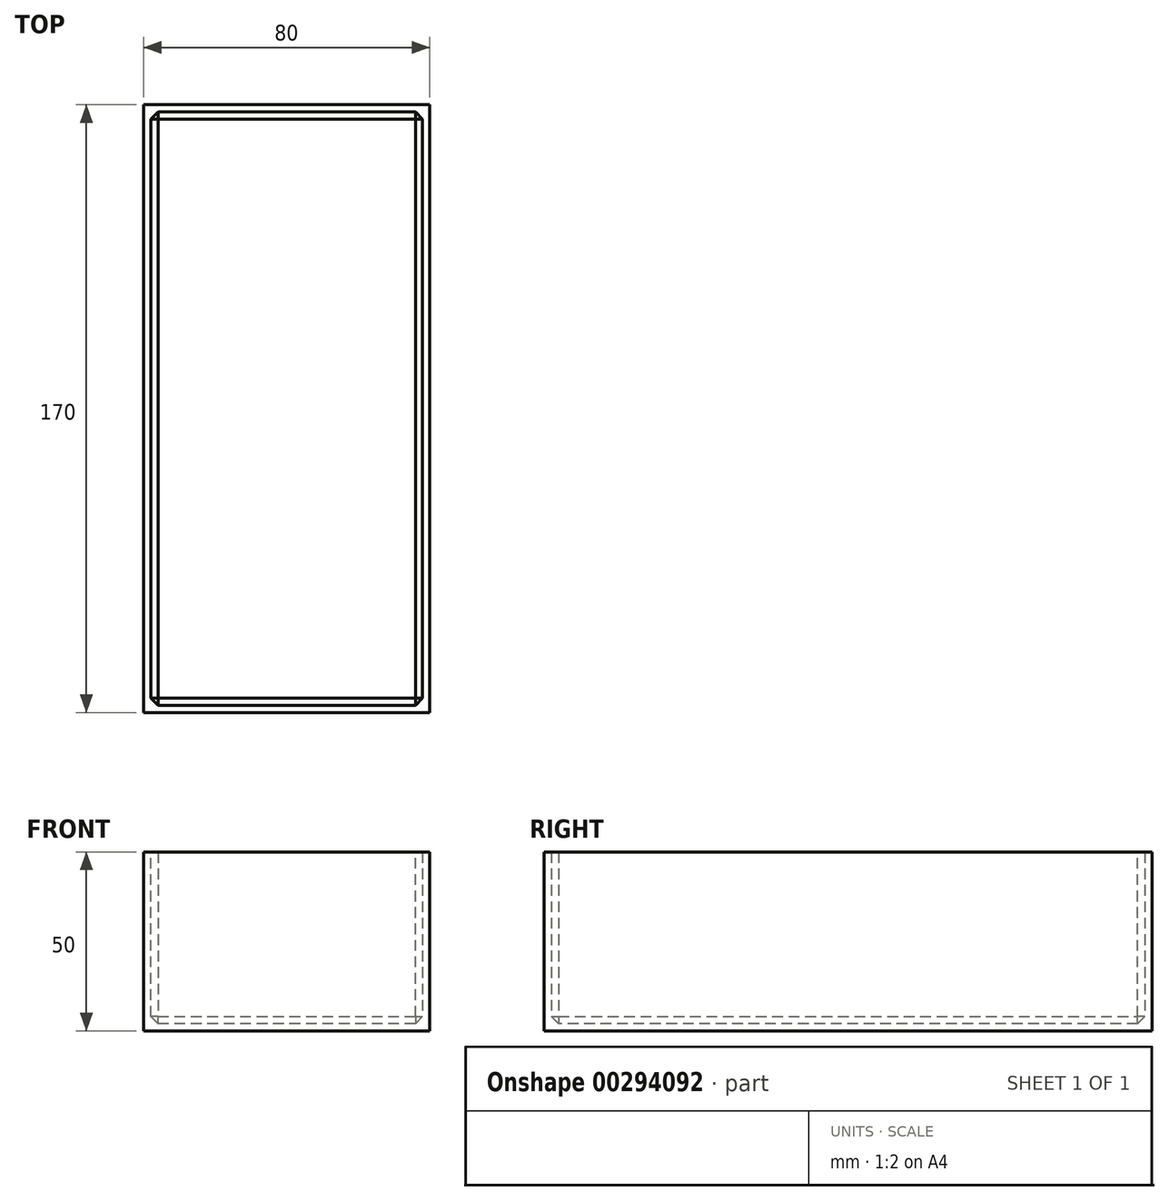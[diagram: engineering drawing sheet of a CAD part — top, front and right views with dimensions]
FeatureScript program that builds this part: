
annotation { "Feature Type Name" : "Feature", "Feature Type Description" : "" }
export const myFeature = defineFeature(function(context is Context, id is Id, definition is map)
    precondition{}
    {
        {
            assignVariable(context, id + "F0", {"name" : "BoxHeight", "anyValue" : 50 * mm});
        }
        {
            var Q0;
            Q0=qCreatedBy(makeId("Top.planeOp"),FACE);
            var sketch = newSketch(context, id + "F1", { "sketchPlane" : qUnion([Q0])});
            skLineSegment(sketch, "E0.bottom", {"start": v(-40, 85) * mm, "end": v(40, 85) * mm});
            skLineSegment(sketch, "E0.top", {"start": v(-40, -85) * mm, "end": v(40, -85) * mm});
            skLineSegment(sketch, "E0.left", {"start": v(-40, 85) * mm, "end": v(-40, -85) * mm});
            skLineSegment(sketch, "E0.right", {"start": v(40, 85) * mm, "end": v(40, -85) * mm});
            skPoint(sketch, "E0.middle", {"position": v(0, 0) * mm});
            skLineSegment(sketch, "E1.0", {"start": v(-38, 83) * mm, "end": v(38, 83) * mm});
            skLineSegment(sketch, "E1.1", {"start": v(-38, 83) * mm, "end": v(-38, -83) * mm});
            skLineSegment(sketch, "E1.2", {"start": v(-38, -83) * mm, "end": v(38, -83) * mm});
            skLineSegment(sketch, "E1.3", {"start": v(38, 83) * mm, "end": v(38, -83) * mm});
            skSolve(sketch);
        }
        {
            var Q0;
            Q0=makeQuery(id+"F1.imprint","IMPRINT",FACE,{"disambiguationData":[TD([[makeQuery(id+"F1.imprint","IMPRINT",EDGE,{"derivedFrom":sQuery(id+"F1.wireOp",EDGE,"E0.bottom")}),-1.0]])]});
            extrude(context, id + "F2", {"entities" : qUnion([Q0]), "depth" : getVariable(context, 'BoxHeight')});
        }
        {
            var Q0;
            Q0=qSketchRegion(id+"F1",true);
            var Q1;
            Q1=makeQuery(id+"F1.imprint","IMPRINT",FACE,{"disambiguationData":[TD([[makeQuery(id+"F1.imprint","IMPRINT",EDGE,{"derivedFrom":sQuery(id+"F1.wireOp",EDGE,"E1.0")}),-1.0]])]});
            extrude(context, id + "F3", {"entities" : qUnion([Q0, Q1]), "operationType" : NewBodyOperationType.ADD, "depth" : 2 * mm});
        }
        {
            var Q0;
            Q0=makeQuery(id+"F3.boolean.opBoolean","INTERSECT",EDGE,{"derivedFrom":[makeQuery(id+"F2.opExtrude","SWEPT_FACE",FACE,{"disambiguationData":[OSD([sQuery(id+"F1.wireOp",EDGE,"E1.0")])]}),makeQuery(id+"F3.opExtrude","CAP_FACE",FACE,{"disambiguationData":[OSD([sQuery(id+"F1.wireOp",EDGE,"E0.bottom"),sQuery(id+"F1.wireOp",EDGE,"E0.top"),sQuery(id+"F1.wireOp",EDGE,"E0.left"),sQuery(id+"F1.wireOp",EDGE,"E0.right")])],"isStart":false})]});
            var Q1;
            Q1=makeQuery(id+"F3.boolean.opBoolean","INTERSECT",EDGE,{"derivedFrom":[makeQuery(id+"F2.opExtrude","SWEPT_FACE",FACE,{"disambiguationData":[OSD([sQuery(id+"F1.wireOp",EDGE,"E1.3")])]}),makeQuery(id+"F3.opExtrude","CAP_FACE",FACE,{"disambiguationData":[OSD([sQuery(id+"F1.wireOp",EDGE,"E0.bottom"),sQuery(id+"F1.wireOp",EDGE,"E0.top"),sQuery(id+"F1.wireOp",EDGE,"E0.left"),sQuery(id+"F1.wireOp",EDGE,"E0.right")])],"isStart":false})]});
            var Q2;
            Q2=makeQuery(id+"F3.boolean.opBoolean","INTERSECT",EDGE,{"derivedFrom":[makeQuery(id+"F2.opExtrude","SWEPT_FACE",FACE,{"disambiguationData":[OSD([sQuery(id+"F1.wireOp",EDGE,"E1.1")])]}),makeQuery(id+"F3.opExtrude","CAP_FACE",FACE,{"disambiguationData":[OSD([sQuery(id+"F1.wireOp",EDGE,"E0.bottom"),sQuery(id+"F1.wireOp",EDGE,"E0.top"),sQuery(id+"F1.wireOp",EDGE,"E0.left"),sQuery(id+"F1.wireOp",EDGE,"E0.right")])],"isStart":false})]});
            var Q3;
            Q3=makeQuery(id+"F3.boolean.opBoolean","INTERSECT",EDGE,{"derivedFrom":[makeQuery(id+"F2.opExtrude","SWEPT_FACE",FACE,{"disambiguationData":[OSD([sQuery(id+"F1.wireOp",EDGE,"E1.2")])]}),makeQuery(id+"F3.opExtrude","CAP_FACE",FACE,{"disambiguationData":[OSD([sQuery(id+"F1.wireOp",EDGE,"E0.bottom"),sQuery(id+"F1.wireOp",EDGE,"E0.top"),sQuery(id+"F1.wireOp",EDGE,"E0.left"),sQuery(id+"F1.wireOp",EDGE,"E0.right")])],"isStart":false})]});
            var Q4;
            Q4=makeQuery(id+"F2.opExtrude","SWEPT_EDGE",EDGE,{"disambiguationData":[OSD([sQuery(id+"F1.wireOp",EDGE,"E1.2"),sQuery(id+"F1.wireOp",EDGE,"E1.3")])]});
            var Q5;
            Q5=makeQuery(id+"F2.opExtrude","SWEPT_EDGE",EDGE,{"disambiguationData":[OSD([sQuery(id+"F1.wireOp",EDGE,"E1.0"),sQuery(id+"F1.wireOp",EDGE,"E1.3")])]});
            var Q6;
            Q6=makeQuery(id+"F2.opExtrude","SWEPT_EDGE",EDGE,{"disambiguationData":[OSD([sQuery(id+"F1.wireOp",EDGE,"E1.0"),sQuery(id+"F1.wireOp",EDGE,"E1.1")])]});
            var Q7;
            Q7=makeQuery(id+"F2.opExtrude","SWEPT_EDGE",EDGE,{"disambiguationData":[OSD([sQuery(id+"F1.wireOp",EDGE,"E1.1"),sQuery(id+"F1.wireOp",EDGE,"E1.2")])]});
            chamfer(context, id + "F4", {"entities" : qUnion([Q0, Q1, Q2, Q3, Q4, Q5, Q6, Q7]), "width" : 2 * mm, "tangentPropagation" : true});
        }
    });
